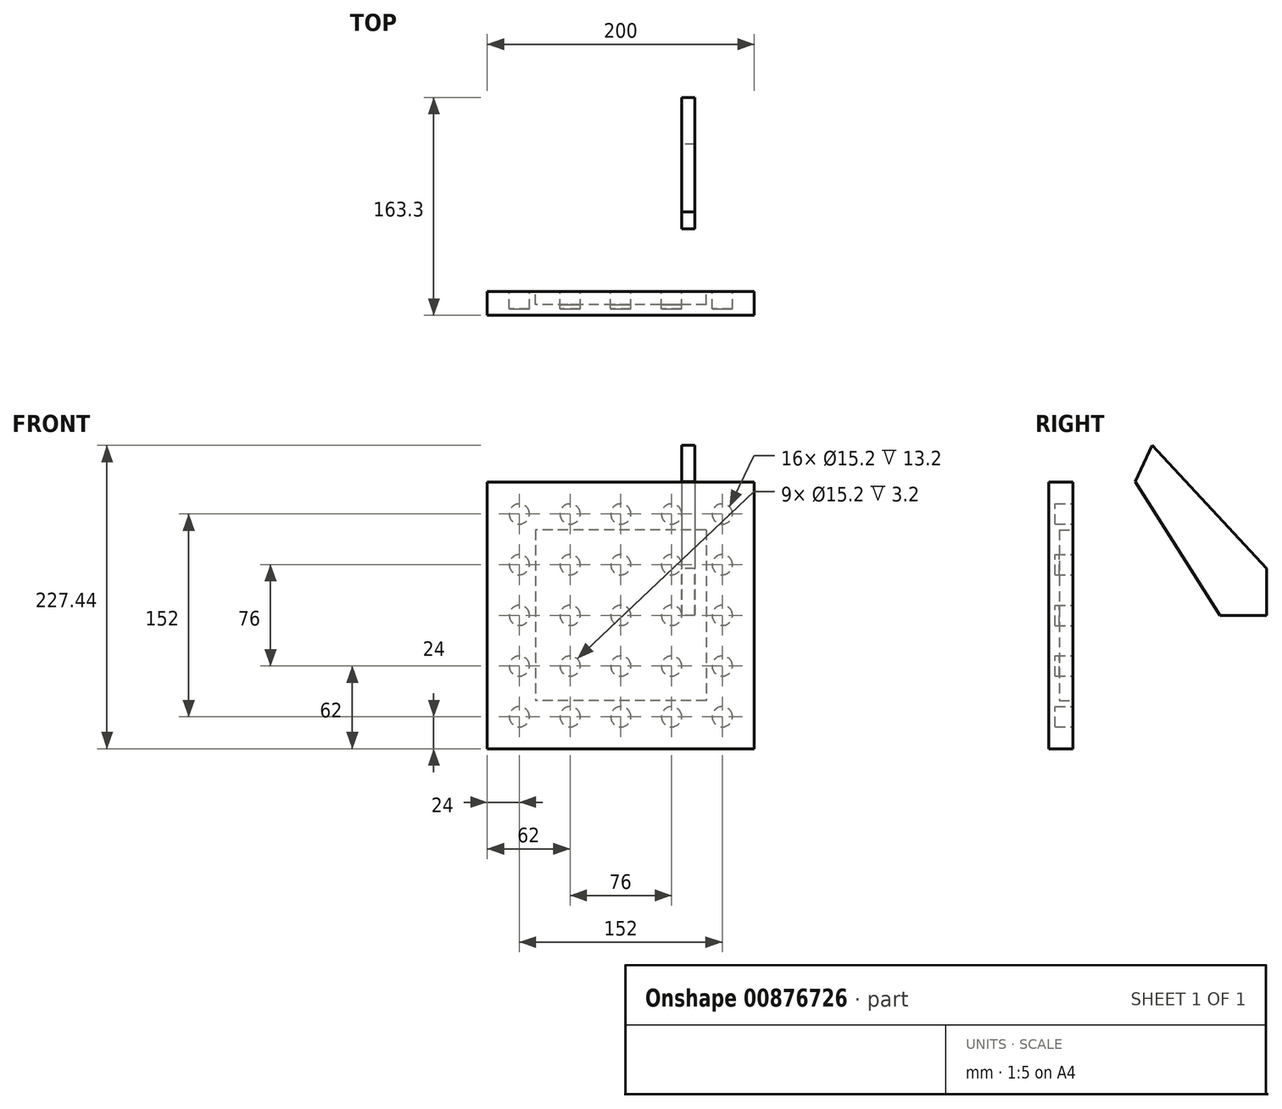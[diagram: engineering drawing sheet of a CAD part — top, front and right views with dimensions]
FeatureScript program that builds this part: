
annotation { "Feature Type Name" : "Feature", "Feature Type Description" : "" }
export const myFeature = defineFeature(function(context is Context, id is Id, definition is map)
    precondition{}
    {
        {
            var Q0;
            Q0=qCreatedBy(makeId("Front.planeOp"),FACE);
            var sketch = newSketch(context, id + "F0", { "sketchPlane" : qUnion([Q0])});
            skLineSegment(sketch, "E0.bottom", {"start": v(-100, 100) * mm, "end": v(100, 100) * mm});
            skLineSegment(sketch, "E0.top", {"start": v(-100, -100) * mm, "end": v(100, -100) * mm});
            skLineSegment(sketch, "E0.left", {"start": v(-100, 100) * mm, "end": v(-100, -100) * mm});
            skLineSegment(sketch, "E0.right", {"start": v(100, 100) * mm, "end": v(100, -100) * mm});
            skCircle(sketch, "E1", {"center": v(-76, 76) * mm, "radius": 7.6 * mm});
            skCircle(sketch, "E2.0.1.0", {"center": v(-76, 38) * mm, "radius": 7.6 * mm});
            skCircle(sketch, "E2.0.2.0", {"center": v(-76, 0) * mm, "radius": 7.6 * mm});
            skCircle(sketch, "E2.0.3.0", {"center": v(-76, -38) * mm, "radius": 7.6 * mm});
            skCircle(sketch, "E2.0.4.0", {"center": v(-76, -76) * mm, "radius": 7.6 * mm});
            skCircle(sketch, "E2.1.0.0", {"center": v(-38, 76) * mm, "radius": 7.6 * mm});
            skCircle(sketch, "E2.1.1.0", {"center": v(-38, 38) * mm, "radius": 7.6 * mm});
            skCircle(sketch, "E2.1.2.0", {"center": v(-38, 0) * mm, "radius": 7.6 * mm});
            skCircle(sketch, "E2.1.3.0", {"center": v(-38, -38) * mm, "radius": 7.6 * mm});
            skCircle(sketch, "E2.1.4.0", {"center": v(-38, -76) * mm, "radius": 7.6 * mm});
            skCircle(sketch, "E2.2.0.0", {"center": v(0, 76) * mm, "radius": 7.6 * mm});
            skCircle(sketch, "E2.2.1.0", {"center": v(0, 38) * mm, "radius": 7.6 * mm});
            skCircle(sketch, "E2.2.2.0", {"center": v(0, 0) * mm, "radius": 7.6 * mm});
            skCircle(sketch, "E2.2.3.0", {"center": v(0, -38) * mm, "radius": 7.6 * mm});
            skCircle(sketch, "E2.2.4.0", {"center": v(0, -76) * mm, "radius": 7.6 * mm});
            skCircle(sketch, "E2.3.0.0", {"center": v(38, 76) * mm, "radius": 7.6 * mm});
            skCircle(sketch, "E2.3.1.0", {"center": v(38, 38) * mm, "radius": 7.6 * mm});
            skCircle(sketch, "E2.3.2.0", {"center": v(38, 0) * mm, "radius": 7.6 * mm});
            skCircle(sketch, "E2.3.3.0", {"center": v(38, -38) * mm, "radius": 7.6 * mm});
            skCircle(sketch, "E2.3.4.0", {"center": v(38, -76) * mm, "radius": 7.6 * mm});
            skCircle(sketch, "E2.4.0.0", {"center": v(76, 76) * mm, "radius": 7.6 * mm});
            skCircle(sketch, "E2.4.1.0", {"center": v(76, 38) * mm, "radius": 7.6 * mm});
            skCircle(sketch, "E2.4.2.0", {"center": v(76, 0) * mm, "radius": 7.6 * mm});
            skCircle(sketch, "E2.4.3.0", {"center": v(76, -38) * mm, "radius": 7.6 * mm});
            skCircle(sketch, "E2.4.4.0", {"center": v(76, -76) * mm, "radius": 7.6 * mm});
            skLineSegment(sketch, "E2.direction1", {"start": v(-76, 76) * mm, "end": v(-38, 76) * mm, "construction": true});
            skLineSegment(sketch, "E2.direction2", {"start": v(-76, 76) * mm, "end": v(-76, 38) * mm, "construction": true});
            skLineSegment(sketch, "E3.bottom", {"start": v(64, 64) * mm, "end": v(-64, 64) * mm});
            skLineSegment(sketch, "E3.top", {"start": v(64, -64) * mm, "end": v(-64, -64) * mm});
            skLineSegment(sketch, "E3.left", {"start": v(64, 64) * mm, "end": v(64, -64) * mm});
            skLineSegment(sketch, "E3.right", {"start": v(-64, 64) * mm, "end": v(-64, -64) * mm});
            skLineSegment(sketch, "E4", {"start": v(-26.4, 64) * mm, "end": v(-64, 11.7) * mm, "construction": true});
            skSolve(sketch);
        }
        {
            var Q0;
            Q0=makeQuery(id+"F0.imprint","IMPRINT",FACE,{"disambiguationData":[TD([[makeQuery(id+"F0.imprint","IMPRINT",EDGE,{"derivedFrom":sQuery(id+"F0.wireOp",EDGE,"E0.bottom")}),-1.0]])]});
            var Q1;
            Q1=makeQuery(id+"F0.imprint","IMPRINT",FACE,{"disambiguationData":[TD([[makeQuery(id+"F0.imprint","IMPRINT",EDGE,{"derivedFrom":sQuery(id+"F0.wireOp",EDGE,"E1")}),1.0]])]});
            var Q2;
            Q2=makeQuery(id+"F0.imprint","IMPRINT",FACE,{"disambiguationData":[TD([[makeQuery(id+"F0.imprint","IMPRINT",EDGE,{"derivedFrom":sQuery(id+"F0.wireOp",EDGE,"E2.0.1.0")}),1.0]])]});
            var Q3;
            Q3=makeQuery(id+"F0.imprint","IMPRINT",FACE,{"disambiguationData":[TD([[makeQuery(id+"F0.imprint","IMPRINT",EDGE,{"derivedFrom":sQuery(id+"F0.wireOp",EDGE,"E2.0.2.0")}),1.0]])]});
            var Q4;
            Q4=makeQuery(id+"F0.imprint","IMPRINT",FACE,{"disambiguationData":[TD([[makeQuery(id+"F0.imprint","IMPRINT",EDGE,{"derivedFrom":sQuery(id+"F0.wireOp",EDGE,"E2.0.3.0")}),1.0]])]});
            var Q5;
            Q5=makeQuery(id+"F0.imprint","IMPRINT",FACE,{"disambiguationData":[TD([[makeQuery(id+"F0.imprint","IMPRINT",EDGE,{"derivedFrom":sQuery(id+"F0.wireOp",EDGE,"E2.0.4.0")}),1.0]])]});
            var Q6;
            Q6=makeQuery(id+"F0.imprint","IMPRINT",FACE,{"disambiguationData":[TD([[makeQuery(id+"F0.imprint","IMPRINT",EDGE,{"derivedFrom":sQuery(id+"F0.wireOp",EDGE,"E2.1.4.0")}),1.0]])]});
            var Q7;
            Q7=makeQuery(id+"F0.imprint","IMPRINT",FACE,{"disambiguationData":[TD([[makeQuery(id+"F0.imprint","IMPRINT",EDGE,{"derivedFrom":sQuery(id+"F0.wireOp",EDGE,"E2.1.3.0")}),1.0]])]});
            var Q8;
            Q8=makeQuery(id+"F0.imprint","IMPRINT",FACE,{"disambiguationData":[TD([[makeQuery(id+"F0.imprint","IMPRINT",EDGE,{"derivedFrom":sQuery(id+"F0.wireOp",EDGE,"E2.1.2.0")}),1.0]])]});
            var Q9;
            Q9=makeQuery(id+"F0.imprint","IMPRINT",FACE,{"disambiguationData":[TD([[makeQuery(id+"F0.imprint","IMPRINT",EDGE,{"derivedFrom":sQuery(id+"F0.wireOp",EDGE,"E2.2.2.0")}),1.0]])]});
            var Q10;
            Q10=makeQuery(id+"F0.imprint","IMPRINT",FACE,{"disambiguationData":[TD([[makeQuery(id+"F0.imprint","IMPRINT",EDGE,{"derivedFrom":sQuery(id+"F0.wireOp",EDGE,"E2.2.1.0")}),1.0]])]});
            var Q11;
            Q11=makeQuery(id+"F0.imprint","IMPRINT",FACE,{"disambiguationData":[TD([[makeQuery(id+"F0.imprint","IMPRINT",EDGE,{"derivedFrom":sQuery(id+"F0.wireOp",EDGE,"E2.2.0.0")}),1.0]])]});
            var Q12;
            Q12=makeQuery(id+"F0.imprint","IMPRINT",FACE,{"disambiguationData":[TD([[makeQuery(id+"F0.imprint","IMPRINT",EDGE,{"derivedFrom":sQuery(id+"F0.wireOp",EDGE,"E2.3.0.0")}),1.0]])]});
            var Q13;
            Q13=makeQuery(id+"F0.imprint","IMPRINT",FACE,{"disambiguationData":[TD([[makeQuery(id+"F0.imprint","IMPRINT",EDGE,{"derivedFrom":sQuery(id+"F0.wireOp",EDGE,"E2.3.1.0")}),1.0]])]});
            var Q14;
            Q14=makeQuery(id+"F0.imprint","IMPRINT",FACE,{"disambiguationData":[TD([[makeQuery(id+"F0.imprint","IMPRINT",EDGE,{"derivedFrom":sQuery(id+"F0.wireOp",EDGE,"E2.3.2.0")}),1.0]])]});
            var Q15;
            Q15=makeQuery(id+"F0.imprint","IMPRINT",FACE,{"disambiguationData":[TD([[makeQuery(id+"F0.imprint","IMPRINT",EDGE,{"derivedFrom":sQuery(id+"F0.wireOp",EDGE,"E2.3.3.0")}),1.0]])]});
            var Q16;
            Q16=makeQuery(id+"F0.imprint","IMPRINT",FACE,{"disambiguationData":[TD([[makeQuery(id+"F0.imprint","IMPRINT",EDGE,{"derivedFrom":sQuery(id+"F0.wireOp",EDGE,"E2.3.4.0")}),1.0]])]});
            var Q17;
            Q17=makeQuery(id+"F0.imprint","IMPRINT",FACE,{"disambiguationData":[TD([[makeQuery(id+"F0.imprint","IMPRINT",EDGE,{"derivedFrom":sQuery(id+"F0.wireOp",EDGE,"E2.4.4.0")}),1.0]])]});
            var Q18;
            Q18=makeQuery(id+"F0.imprint","IMPRINT",FACE,{"disambiguationData":[TD([[makeQuery(id+"F0.imprint","IMPRINT",EDGE,{"derivedFrom":sQuery(id+"F0.wireOp",EDGE,"E2.4.3.0")}),1.0]])]});
            var Q19;
            Q19=makeQuery(id+"F0.imprint","IMPRINT",FACE,{"disambiguationData":[TD([[makeQuery(id+"F0.imprint","IMPRINT",EDGE,{"derivedFrom":sQuery(id+"F0.wireOp",EDGE,"E2.4.1.0")}),1.0]])]});
            var Q20;
            Q20=makeQuery(id+"F0.imprint","IMPRINT",FACE,{"disambiguationData":[TD([[makeQuery(id+"F0.imprint","IMPRINT",EDGE,{"derivedFrom":sQuery(id+"F0.wireOp",EDGE,"E2.4.0.0")}),1.0]])]});
            var Q21;
            Q21=makeQuery(id+"F0.imprint","IMPRINT",FACE,{"disambiguationData":[TD([[makeQuery(id+"F0.imprint","IMPRINT",EDGE,{"derivedFrom":sQuery(id+"F0.wireOp",EDGE,"E2.1.0.0")}),1.0]])]});
            var Q22;
            Q22=makeQuery(id+"F0.imprint","IMPRINT",FACE,{"disambiguationData":[TD([[makeQuery(id+"F0.imprint","IMPRINT",EDGE,{"derivedFrom":sQuery(id+"F0.wireOp",EDGE,"E2.2.3.0")}),1.0]])]});
            var Q23;
            Q23=makeQuery(id+"F0.imprint","IMPRINT",FACE,{"disambiguationData":[TD([[makeQuery(id+"F0.imprint","IMPRINT",EDGE,{"derivedFrom":sQuery(id+"F0.wireOp",EDGE,"E2.2.4.0")}),1.0]])]});
            var Q24;
            Q24=makeQuery(id+"F0.imprint","IMPRINT",FACE,{"disambiguationData":[TD([[makeQuery(id+"F0.imprint","IMPRINT",EDGE,{"derivedFrom":sQuery(id+"F0.wireOp",EDGE,"E2.4.2.0")}),1.0]])]});
            var Q25;
            Q25=makeQuery(id+"F0.imprint","IMPRINT",FACE,{"disambiguationData":[TD([[makeQuery(id+"F0.imprint","IMPRINT",EDGE,{"derivedFrom":sQuery(id+"F0.wireOp",EDGE,"E2.1.1.0")}),1.0]])]});
            var Q26;
            Q26=makeQuery(id+"F0.imprint","IMPRINT",FACE,{"disambiguationData":[TD([[makeQuery(id+"F0.imprint","IMPRINT",EDGE,{"derivedFrom":sQuery(id+"F0.wireOp",EDGE,"JodtR8iw-KzQY-ANBh-eKrK-CL3xPLxFBDxO.bottom")}),1.0]])]});
            var Q27;
            Q27=makeQuery(id+"F0.imprint","IMPRINT",FACE,{"disambiguationData":[TD([[makeQuery(id+"F0.imprint","IMPRINT",EDGE,{"derivedFrom":sQuery(id+"F0.wireOp",EDGE,"GZYiYnze-6Z1p-Ccex-q3jf-NM6sBKju0V84")}),1.0]])]});
            var Q28;
            Q28=makeQuery(id+"F0.imprint","IMPRINT",FACE,{"disambiguationData":[TD([[makeQuery(id+"F0.imprint","IMPRINT",EDGE,{"derivedFrom":sQuery(id+"F0.wireOp",EDGE,"E2.1.1.0")}),-1.0]])]});
            extrude(context, id + "F1", {"entities" : qUnion([Q0, Q1, Q2, Q3, Q4, Q5, Q6, Q7, Q8, Q9, Q10, Q11, Q12, Q13, Q14, Q15, Q16, Q17, Q18, Q19, Q20, Q21, Q22, Q23, Q24, Q25, Q26, Q27, Q28]), "depth" : 18 * mm, "offsetDistance" : 25 * mm});
        }
        {
            var Q0;
            Q0=makeQuery(id+"F0.imprint","IMPRINT",FACE,{"disambiguationData":[TD([[makeQuery(id+"F0.imprint","IMPRINT",EDGE,{"derivedFrom":sQuery(id+"F0.wireOp",EDGE,"E2.1.1.0")}),-1.0]])]});
            extrude(context, id + "F2", {"entities" : qUnion([Q0]), "operationType" : NewBodyOperationType.REMOVE, "depth" : 10 * mm, "offsetDistance" : 25 * mm});
        }
        {
            var Q0;
            Q0=makeQuery(id+"F0.imprint","IMPRINT",FACE,{"disambiguationData":[TD([[makeQuery(id+"F0.imprint","IMPRINT",EDGE,{"derivedFrom":sQuery(id+"F0.wireOp",EDGE,"E2.4.0.0")}),1.0]])]});
            var Q1;
            Q1=makeQuery(id+"F0.imprint","IMPRINT",FACE,{"disambiguationData":[TD([[makeQuery(id+"F0.imprint","IMPRINT",EDGE,{"derivedFrom":sQuery(id+"F0.wireOp",EDGE,"E2.3.0.0")}),1.0]])]});
            var Q2;
            Q2=makeQuery(id+"F0.imprint","IMPRINT",FACE,{"disambiguationData":[TD([[makeQuery(id+"F0.imprint","IMPRINT",EDGE,{"derivedFrom":sQuery(id+"F0.wireOp",EDGE,"E2.3.1.0")}),1.0]])]});
            var Q3;
            Q3=makeQuery(id+"F0.imprint","IMPRINT",FACE,{"disambiguationData":[TD([[makeQuery(id+"F0.imprint","IMPRINT",EDGE,{"derivedFrom":sQuery(id+"F0.wireOp",EDGE,"E2.4.1.0")}),1.0]])]});
            var Q4;
            Q4=makeQuery(id+"F0.imprint","IMPRINT",FACE,{"disambiguationData":[TD([[makeQuery(id+"F0.imprint","IMPRINT",EDGE,{"derivedFrom":sQuery(id+"F0.wireOp",EDGE,"E2.4.2.0")}),1.0]])]});
            var Q5;
            Q5=makeQuery(id+"F0.imprint","IMPRINT",FACE,{"disambiguationData":[TD([[makeQuery(id+"F0.imprint","IMPRINT",EDGE,{"derivedFrom":sQuery(id+"F0.wireOp",EDGE,"E2.4.3.0")}),1.0]])]});
            var Q6;
            Q6=makeQuery(id+"F0.imprint","IMPRINT",FACE,{"disambiguationData":[TD([[makeQuery(id+"F0.imprint","IMPRINT",EDGE,{"derivedFrom":sQuery(id+"F0.wireOp",EDGE,"E2.3.3.0")}),1.0]])]});
            var Q7;
            Q7=makeQuery(id+"F0.imprint","IMPRINT",FACE,{"disambiguationData":[TD([[makeQuery(id+"F0.imprint","IMPRINT",EDGE,{"derivedFrom":sQuery(id+"F0.wireOp",EDGE,"E2.3.2.0")}),1.0]])]});
            var Q8;
            Q8=makeQuery(id+"F0.imprint","IMPRINT",FACE,{"disambiguationData":[TD([[makeQuery(id+"F0.imprint","IMPRINT",EDGE,{"derivedFrom":sQuery(id+"F0.wireOp",EDGE,"E2.4.4.0")}),1.0]])]});
            var Q9;
            Q9=makeQuery(id+"F0.imprint","IMPRINT",FACE,{"disambiguationData":[TD([[makeQuery(id+"F0.imprint","IMPRINT",EDGE,{"derivedFrom":sQuery(id+"F0.wireOp",EDGE,"E2.3.4.0")}),1.0]])]});
            var Q10;
            Q10=makeQuery(id+"F0.imprint","IMPRINT",FACE,{"disambiguationData":[TD([[makeQuery(id+"F0.imprint","IMPRINT",EDGE,{"derivedFrom":sQuery(id+"F0.wireOp",EDGE,"E2.2.4.0")}),1.0]])]});
            var Q11;
            Q11=makeQuery(id+"F0.imprint","IMPRINT",FACE,{"disambiguationData":[TD([[makeQuery(id+"F0.imprint","IMPRINT",EDGE,{"derivedFrom":sQuery(id+"F0.wireOp",EDGE,"E2.2.3.0")}),1.0]])]});
            var Q12;
            Q12=makeQuery(id+"F0.imprint","IMPRINT",FACE,{"disambiguationData":[TD([[makeQuery(id+"F0.imprint","IMPRINT",EDGE,{"derivedFrom":sQuery(id+"F0.wireOp",EDGE,"E2.2.2.0")}),1.0]])]});
            var Q13;
            Q13=makeQuery(id+"F0.imprint","IMPRINT",FACE,{"disambiguationData":[TD([[makeQuery(id+"F0.imprint","IMPRINT",EDGE,{"derivedFrom":sQuery(id+"F0.wireOp",EDGE,"E2.2.1.0")}),1.0]])]});
            var Q14;
            Q14=makeQuery(id+"F0.imprint","IMPRINT",FACE,{"disambiguationData":[TD([[makeQuery(id+"F0.imprint","IMPRINT",EDGE,{"derivedFrom":sQuery(id+"F0.wireOp",EDGE,"E2.1.0.0")}),1.0]])]});
            var Q15;
            Q15=makeQuery(id+"F0.imprint","IMPRINT",FACE,{"disambiguationData":[TD([[makeQuery(id+"F0.imprint","IMPRINT",EDGE,{"derivedFrom":sQuery(id+"F0.wireOp",EDGE,"E2.2.0.0")}),1.0]])]});
            var Q16;
            Q16=makeQuery(id+"F0.imprint","IMPRINT",FACE,{"disambiguationData":[TD([[makeQuery(id+"F0.imprint","IMPRINT",EDGE,{"derivedFrom":sQuery(id+"F0.wireOp",EDGE,"E2.1.1.0")}),1.0]])]});
            var Q17;
            Q17=makeQuery(id+"F0.imprint","IMPRINT",FACE,{"disambiguationData":[TD([[makeQuery(id+"F0.imprint","IMPRINT",EDGE,{"derivedFrom":sQuery(id+"F0.wireOp",EDGE,"E2.1.2.0")}),1.0]])]});
            var Q18;
            Q18=makeQuery(id+"F0.imprint","IMPRINT",FACE,{"disambiguationData":[TD([[makeQuery(id+"F0.imprint","IMPRINT",EDGE,{"derivedFrom":sQuery(id+"F0.wireOp",EDGE,"E2.1.3.0")}),1.0]])]});
            var Q19;
            Q19=makeQuery(id+"F0.imprint","IMPRINT",FACE,{"disambiguationData":[TD([[makeQuery(id+"F0.imprint","IMPRINT",EDGE,{"derivedFrom":sQuery(id+"F0.wireOp",EDGE,"E2.1.4.0")}),1.0]])]});
            var Q20;
            Q20=makeQuery(id+"F0.imprint","IMPRINT",FACE,{"disambiguationData":[TD([[makeQuery(id+"F0.imprint","IMPRINT",EDGE,{"derivedFrom":sQuery(id+"F0.wireOp",EDGE,"E2.0.4.0")}),1.0]])]});
            var Q21;
            Q21=makeQuery(id+"F0.imprint","IMPRINT",FACE,{"disambiguationData":[TD([[makeQuery(id+"F0.imprint","IMPRINT",EDGE,{"derivedFrom":sQuery(id+"F0.wireOp",EDGE,"E2.0.3.0")}),1.0]])]});
            var Q22;
            Q22=makeQuery(id+"F0.imprint","IMPRINT",FACE,{"disambiguationData":[TD([[makeQuery(id+"F0.imprint","IMPRINT",EDGE,{"derivedFrom":sQuery(id+"F0.wireOp",EDGE,"E2.0.2.0")}),1.0]])]});
            var Q23;
            Q23=makeQuery(id+"F0.imprint","IMPRINT",FACE,{"disambiguationData":[TD([[makeQuery(id+"F0.imprint","IMPRINT",EDGE,{"derivedFrom":sQuery(id+"F0.wireOp",EDGE,"E2.0.1.0")}),1.0]])]});
            var Q24;
            Q24=makeQuery(id+"F0.imprint","IMPRINT",FACE,{"disambiguationData":[TD([[makeQuery(id+"F0.imprint","IMPRINT",EDGE,{"derivedFrom":sQuery(id+"F0.wireOp",EDGE,"E1")}),1.0]])]});
            extrude(context, id + "F3", {"entities" : qUnion([Q0, Q1, Q2, Q3, Q4, Q5, Q6, Q7, Q8, Q9, Q10, Q11, Q12, Q13, Q14, Q15, Q16, Q17, Q18, Q19, Q20, Q21, Q22, Q23, Q24]), "operationType" : NewBodyOperationType.REMOVE, "depth" : 13.2 * mm, "offsetDistance" : 25 * mm});
        }
        {
            var Q0;
            Q0=qCreatedBy(makeId("Right.planeOp"),FACE);
            var sketch = newSketch(context, id + "F4", { "sketchPlane" : qUnion([Q0])});
            skLineSegment(sketch, "E5.left", {"start": v(46.75, 100.25) * mm, "end": v(110.3, 0) * mm});
            skLineSegment(sketch, "E6", {"start": v(59.43, 127.44) * mm, "end": v(46.75, 100.25) * mm});
            skLineSegment(sketch, "E7", {"start": v(145.3, 0) * mm, "end": v(110.3, 0) * mm});
            skLineSegment(sketch, "E8", {"start": v(0, 0) * mm, "end": v(71.22, 152.72) * mm, "construction": true});
            skPoint(sketch, "E9", {"position": v(53.09, 113.85) * mm});
            skLineSegment(sketch, "E10", {"start": v(68.42, 130.16) * mm, "end": v(64.12, 120.95) * mm});
            skLineSegment(sketch, "E11", {"start": v(63.08, 118.72) * mm, "end": v(56.15, 103.85) * mm});
            skLineSegment(sketch, "E12", {"start": v(54.43, 100.17) * mm, "end": v(51.2, 93.23) * mm});
            skPoint(sketch, "E13.visualSharp", {"position": v(56.15, 103.85) * mm});
            skLineSegment(sketch, "E14", {"start": v(70.7, 135.04) * mm, "end": v(68.42, 130.16) * mm});
            skLineSegment(sketch, "E15", {"start": v(44.47, 95.37) * mm, "end": v(46.75, 100.25) * mm});
            skLineSegment(sketch, "E16", {"start": v(70.7, 135.04) * mm, "end": v(7.72, 0) * mm, "construction": true});
            skLineSegment(sketch, "E17", {"start": v(145.3, 0) * mm, "end": v(145.3, 35) * mm});
            skLineSegment(sketch, "E18", {"start": v(59.43, 127.44) * mm, "end": v(145.3, 35) * mm});
            skSolve(sketch);
        }
        {
            var Q0;
            {var subQ4=sQuery(id+"F4.wireOp",EDGE,"E6");Q0=makeQuery(id+"F4.imprint","IMPRINT",FACE,{"disambiguationData":[TD([[makeQuery(id+"F4.imprint","IMPRINT",EDGE,{"derivedFrom":subQ4}),1.0]])]});}
            var Q1;
            {var subQ0=sQuery(id+"F4.wireOp",EDGE,"C8OtKQTw-gj23-F0Sa-SCu7-s4atycH0EDzZ");Q1=makeQuery(id+"F4.imprint","IMPRINT",FACE,{"disambiguationData":[TD([[makeQuery(id+"F4.imprint","IMPRINT",EDGE,{"derivedFrom":subQ0}),-1.0]])]});}
            var Q2;
            {var subQ0=sQuery(id+"F4.wireOp",EDGE,"jpJnjbxq-8uQn-xHV8-NdU1-g7NnKgzqhGBX");Q2=makeQuery(id+"F4.imprint","IMPRINT",FACE,{"disambiguationData":[TD([[makeQuery(id+"F4.imprint","IMPRINT",EDGE,{"derivedFrom":subQ0}),-1.0]])]});}
            var Q3;
            {var subQ0=sQuery(id+"F4.wireOp",EDGE,"SipZrYRY-YJ4p-PDh7-1GNw-encrGY5vpzvW");Q3=makeQuery(id+"F4.imprint","IMPRINT",FACE,{"disambiguationData":[TD([[makeQuery(id+"F4.imprint","IMPRINT",EDGE,{"derivedFrom":subQ0}),-1.0]])]});}
            var Q4;
            {var subQ2=sQuery(id+"F4.wireOp",EDGE,"UzdOtamn-eJ4e-PsxF-iLEW-jHttbTvfivtN");Q4=makeQuery(id+"F4.imprint","IMPRINT",FACE,{"disambiguationData":[TD([[makeQuery(id+"F4.imprint","IMPRINT",EDGE,{"derivedFrom":subQ2}),-1.0]])]});}
            extrude(context, id + "F5", {"entities" : qUnion([Q0, Q1, Q2, Q3, Q4]), "depth" : 55.5 * mm, "offsetDistance" : 25 * mm, "hasSecondDirection" : true, "secondDirectionOppositeDirection" : false, "secondDirectionDepth" : 45.5 * mm});
        }
    });
